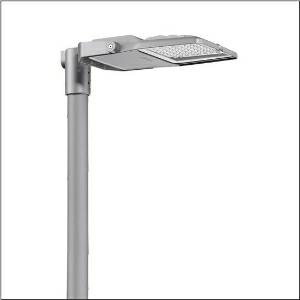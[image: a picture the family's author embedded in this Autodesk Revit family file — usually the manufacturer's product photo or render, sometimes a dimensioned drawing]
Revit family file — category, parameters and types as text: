
# Revit family: floodlight_fl_21_iq_mini___pl61_5xa7772c2c3a_f769
name_source: partatom
category: Lighting Fixtures
units: mm (PartAtom-declared; Revit-internal decimal feet)

## family parameters
Cut with Voids When Loaded = No
Host = Face
Light Source = No
Part Type = Normal
Room Calculation Point = No
Round Connector Dimension = Use Diameter
Shared = No

## types (1)
- --- (1 x LED, 11980 lm, 87.2 W, 3000K)
    Apparent Load = 87 VA
    CIE Flux Codes = 33 65 98 100 100
    Color Rendering = 70
    Color Temperature = 3000K
    Default Elevation = 1800 mm
    Description = Floodlight FL 21 iQ mini, floodlight, primary light control with lens, of PMMA, primary optical cover: protective disc, of toughened safety glass, transparent, light distribution: PL61, light emission: direct distribution, installation type: surface-mounted, LED, High Power LED, rated luminous flux: 11.980lm, luminous efficacy: 137lm/W, light colour: 730, colour temperature: 3000K, control gear: iQ Street-Remote/DALI, control: Auto-Match, Temp-Guard, Night-Set, Smart-Wire, Desk-Remote (wireless, voltage-free reading and setting of iQ features in the workshop via application-optimized NFC function/RFID function), optimised constant luminous flux control (CLO 2.0), Light-Fading, Lumen-Switch, with terminal, 6-pole, mains connection: 220..240V, AC, 50/60Hz, start of lifetime: 87W, end of service life: 92W, reduction: 40W, luminaire housing, of diecast aluminium, powder-coated, Siteco® metallic grey (DB 702S), corrosivity category C5 mid according to DIN EN ISO 12944, suitable for swimming pools, chlorine-resistant, sealing non-destructively replaceable, please order mast flange separately, mast bracket, of steel, galvanised, powder-coated, protection rating (complete): IP66, insulation class (complete): insulation class II (safety insulation), certification: CE, ENEC, VDE, protection symbol: D, impact resistance: IK08, permissible operating ambient temperature: -40..+40°C, permissible operating ambient temperature for outdoor applications: -40..+50°C, standard: DIN EN 12944, LABS conformity tested according to VDMA 24364:2018-05, packaging unit: 1 piece

Light Distribution: PL61
    Height = 70 mm
    Lamp = 1 x LED
    Lamp Light Flux = 11980 lm
    Lamp Power = 87.2 W
    Lamp count = 1
    Length = 485 mm
    Luminous efficacy = 137 lm/W
    Manufacturer = Siteco
    ModVariant = No
    Model = 5XA7772C2C3A
    Number of Poles = 1
    OnlyDefault = Yes
    Power Factor = 1
    Product Name = Floodlight FL 21 iQ mini | PL61
    Product group = floodlight | pylon annexe
    ProductGroupID = 6201
    Protection Class = Protection class II
    Protection Degree = IP 66
    RLX_Detail_Level = 1
    RLX_Emergency_Light_Flux = 0 lm
    RLX_Emergency_Type = 0
    RLX_Emergency_Type_DB = No
    RlxData = <blob elided: 101485 chars, md5=06dd7722>
    Socket = socket
    Standby Power = 0 W
    System Light Flux = 11980 lm
    System Power = 87 W
    Type Comments = factory setting: luminous flux: 100 % | dim-lin: 254 | 456 mA
    Type Image = l_1007125.jpg
    URL = http://relux.com
    VarID = @adj_194517
    Voltage = 0 V
    Weight = 0.00 kg
    Width = 337 mm

## geometry (parser evidence)
native form markers: Blend x4, Sweep x11
no freeform markers — native parametric forms only
